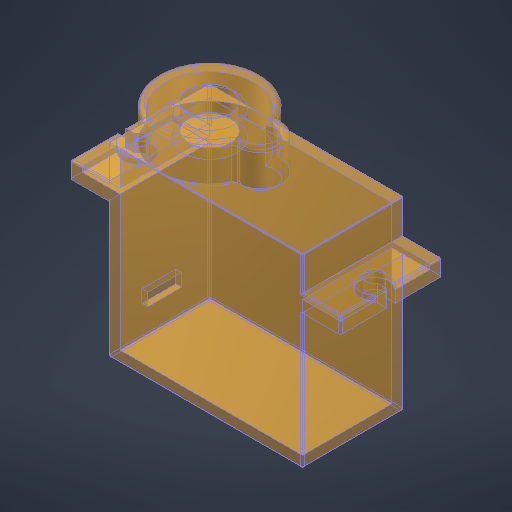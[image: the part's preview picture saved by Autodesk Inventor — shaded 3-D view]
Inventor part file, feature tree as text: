
AUTODESK INVENTOR PART (.ipt)
format: ipt  version: 2025.3 (Build 293356000, 356)  size: 515,584 bytes
history: native  units: in
note: dims shown in document units (in); Inventor stores cm internally (conversion verified against a paired STEP export)
features: fillet x21, extrude x8, sketch x5, shell x1
ambient origin geometry x8: Origin, YZ Plane, XZ Plane, XY Plane, X Axis, Y Axis, Z Axis, Center Point
bodies: Solid1 (feature_tree)
feature tree (35):
  extrude  "Extrusion1"  Depth=0.6299in
  extrude  "Extrusion2"  Depth=0.4724in
  extrude  "Extrusion3"  Depth=0.0787in TaperAngle=0.0deg
  extrude  "Extrusion4"  Depth=0.4724in
  extrude  "Extrusion5"  Depth=0.0787in
  extrude  "Extrusion6"  Depth=0.0079in TaperAngle=0.0deg
  extrude  "Extrusion7"  Depth=0.0079in TaperAngle=0.0deg
  shell  "Shell1"  Thickness=0.1654in
  extrude  "Extrusion8"  Depth=0.0079in
  fillet  "Fillet1"  Radius=0.1181in
  fillet  "Fillet2"  Radius=0.0276in
  fillet  "Fillet3"  Radius=0.1575in
  fillet  "Fillet4"  Radius=0.0591in
  fillet  "Fillet5"  Radius=0.1378in
  fillet  "Fillet6"  Radius=0.1181in
  fillet  "Fillet7"  Radius=0.0197in
  fillet  "Fillet8"  Radius=0.0197in
  fillet  "Fillet9"  Radius=0.0197in
  fillet  "Fillet10"  Radius=0.0079in
  fillet  "Fillet11"  Radius=0.0079in
  fillet  "Fillet12"  Radius=0.0079in
  fillet  "Fillet13"  Radius=0.0079in
  fillet  "Fillet14"  Radius=0.0079in
  fillet  "Fillet15"  Radius=0.0079in
  fillet  "Fillet16"  Radius=0.0079in
  fillet  "Fillet17"  Radius=0.0079in
  fillet  "Fillet18"  Radius=0.0079in
  fillet  "Fillet19"  Radius=0.0079in
  fillet  "Fillet20"  Radius=0.0079in
  fillet  "Fillet21"  Radius=0.0079in
  sketch  "Sketch2"  dims[d0=0.9055in d1=0.6299in]
  sketch  "Sketch4"  dims[d2=0.4724in d3=0.0in d4=1.2598in]
  sketch  "Sketch5"  dims[d5=0.4724in d6=0.0787in d7=0.0in]
  sketch  "Sketch6"  dims[d8=0.9055in d9=0.4724in]
  sketch  "Sketch8"  dims[d10=0.1575in d11=0.0in d12=0.0787in d16=0.1654in d17=0.0in d22=0.1654in d23=0.0in d27=0.1654in d28=0.0in d29=0.1969in d30=0.1181in d31=0.0in d32=0.0276in d33=0.1575in d34=0.0591in d35=0.1378in d36=0.1181in d37=0.0in d38=0.0197in d39=0.0197in d40=0.0197in d41=0.0079in d42=0.0079in d43=0.0079in d44=0.0079in d45=0.0079in d46=0.0079in d47=0.0079in d48=0.0079in d49=0.0079in d50=0.0079in d51=0.0079in d52=0.0079in d53=0.0039in d54=0.0039in d55=0.0079in d56=0.0079in d57=0.0079in d58=0.0079in]
